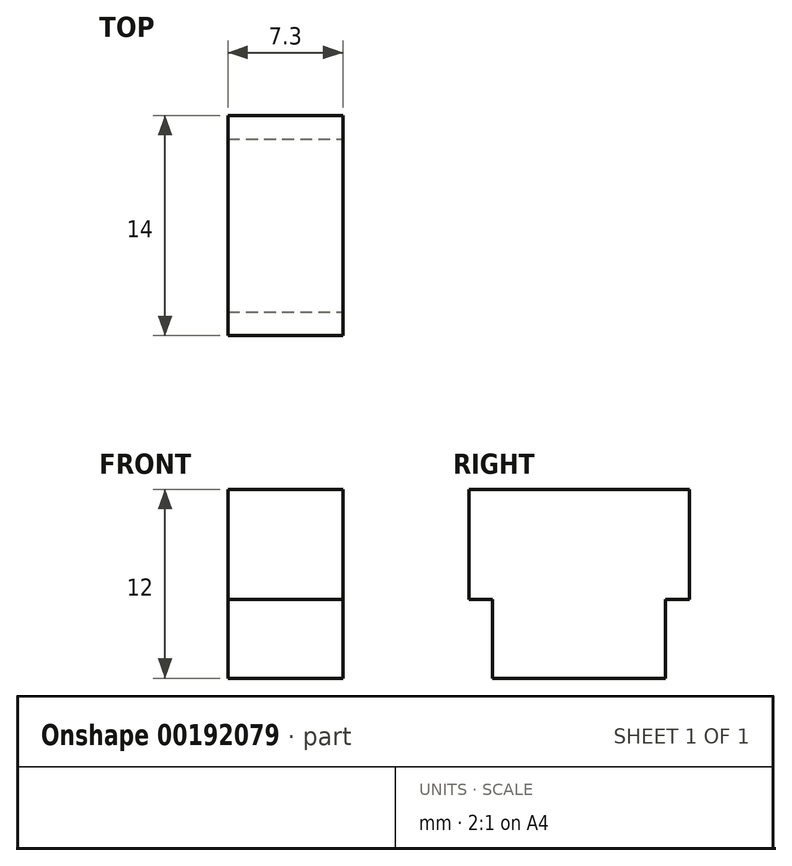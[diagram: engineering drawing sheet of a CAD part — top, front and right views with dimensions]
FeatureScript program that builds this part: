
annotation { "Feature Type Name" : "Feature", "Feature Type Description" : "" }
export const myFeature = defineFeature(function(context is Context, id is Id, definition is map)
    precondition{}
    {
        {
            var Q0;
            Q0=qCreatedBy(makeId("Top.planeOp"),FACE);
            var sketch = newSketch(context, id + "F0", { "sketchPlane" : qUnion([Q0])});
            skLineSegment(sketch, "E0.bottom", {"start": v(3.65, -7) * mm, "end": v(-3.65, -7) * mm});
            skLineSegment(sketch, "E0.top", {"start": v(3.65, 7) * mm, "end": v(-3.65, 7) * mm});
            skLineSegment(sketch, "E0.left", {"start": v(3.65, -7) * mm, "end": v(3.65, 7) * mm});
            skLineSegment(sketch, "E0.right", {"start": v(-3.65, -7) * mm, "end": v(-3.65, 7) * mm});
            skPoint(sketch, "E0.middle", {"position": v(0, 0) * mm});
            skSolve(sketch);
        }
        {
            var Q0;
            Q0 = qSketchRegion(id + "F0", true);
            extrude(context, id + "F1", {"entities" : qUnion([Q0]), "depth" : 12 * mm});
        }
        {
            var Q0;
            Q0=makeQuery(id+"F1.opExtrude","SWEPT_FACE",FACE,{"disambiguationData":[OSD([sQuery(id+"F0.wireOp",EDGE,"E0.left")])]});
            var sketch = newSketch(context, id + "F2", { "sketchPlane" : qUnion([Q0])});
            skLineSegment(sketch, "E1.bottom", {"start": v(-7, 0) * mm, "end": v(-5.5, 0) * mm});
            skLineSegment(sketch, "E1.top", {"start": v(-7, 5) * mm, "end": v(-5.5, 5) * mm});
            skLineSegment(sketch, "E1.left", {"start": v(-7, 0) * mm, "end": v(-7, 5) * mm});
            skLineSegment(sketch, "E1.right", {"start": v(-5.5, 0) * mm, "end": v(-5.5, 5) * mm});
            skLineSegment(sketch, "E2.bottom", {"start": v(7, 0) * mm, "end": v(5.5, 0) * mm});
            skLineSegment(sketch, "E2.top", {"start": v(7, 5) * mm, "end": v(5.5, 5) * mm});
            skLineSegment(sketch, "E2.left", {"start": v(7, 0) * mm, "end": v(7, 5) * mm});
            skLineSegment(sketch, "E2.right", {"start": v(5.5, 0) * mm, "end": v(5.5, 5) * mm});
            skSolve(sketch);
        }
        {
            var Q0;
            Q0 = qSketchRegion(id + "F2", true);
            extrude(context, id + "F3", {"entities" : qUnion([Q0]), "operationType" : NewBodyOperationType.REMOVE, "oppositeDirection" : true, "depth" : 25 * mm});
        }
    });
